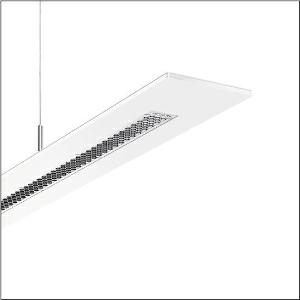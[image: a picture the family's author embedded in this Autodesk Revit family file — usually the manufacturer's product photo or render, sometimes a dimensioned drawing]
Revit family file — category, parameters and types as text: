
# Revit family: arktika_r__21_5mb251dl30830_c5c6
name_source: partatom
category: Lighting Fixtures
units: mm (PartAtom-declared; Revit-internal decimal feet)

## family parameters
Cut with Voids When Loaded = No
Host = Face
Light Source = No
Part Type = Normal
Room Calculation Point = No
Round Connector Dimension = Use Diameter
Shared = No

## types (1)
- --- (1 x LED 3000K / CRI = 80 (unbekannt), 4050 lm, 3000K)
    Apparent Load = 34 VA
    CIE Flux Codes = 81 100 100 79 100
    Color Rendering = 80
    Color Temperature = 3000K
    Default Elevation = 1800 mm
    Description = Arktika® 21, office luminaire, primary anti-glare with honeycomb louvre, of plastic, aluminium vaporised, highly specular, light emission: direct/indirect distribution, primary light characteristic: symmetric, installation type: suspended mounting, LED, rated luminous flux: 4.050lm, luminous efficacy: 120lm/W, light colour: 830, colour temperature: 3000K, control gear: ECG DALI, with terminal, 3+2-pole, max. 2.5mm², mains connection: 220..240V, AC, 50/60Hz, rated input power: 34W, housing, of aluminium, powder-coated, traffic white (RAL 9016), 1-length, length: 1.250mm, width: 120mm, height: 8mm, protection rating (complete): IP20, insulation class (complete): insulation class II (safety insulation), certification: CE, ENEC, VDE, packaging unit: 1 piece
    Height = 8 mm  [stored 0.0262467 ft]
    Lamp = 1 x LED 3000K / CRI >= 80 (unbekannt)
    Lamp Light Flux = 4050 lm
    Lamp count = 1
    Length = 1250 mm
    Luminous efficacy = 120 lm/W
    Manufacturer = Siteco
    ModVariant = No
    Model = 5MB251DL30830
    Mounting Place = Ceiling
    Mounting Type = Pendant
    Number of Poles = 1
    OnlyDefault = Yes
    Power Factor = 1
    Product Name = Arktika® 21
    Product group = office luminaire | ceiling pendant
    ProductGroupID = 902
    Protection Class = Protection class II
    Protection Degree = IP 20
    RLX_Detail_Level = 1
    RLX_Emergency_Light_Flux = 0 lm
    RLX_Emergency_Type = 0
    RLX_Emergency_Type_DB = No
    RlxData = <blob elided: 39281 chars, md5=9dfea284>
    Socket = socket
    Standby Power = 0 W
    System Light Flux = 4050 lm
    System Power = 34 W
    Type Comments = factory setting: luminous flux: 100 % | dim-lin: 254 | 665 mA
    Type Image = l_1006128.jpg
    URL = http://relux.com
    VarID = @adj_148893
    Voltage = 0 V
    Weight = 0.00 kg
    Width = 120 mm

note: [stored X ft] marks values corroborated as IEEE doubles in the binary element streams (Revit-internal decimal feet)

## geometry (parser evidence)
native form markers: Blend x4, Sweep x10
no freeform markers — native parametric forms only
